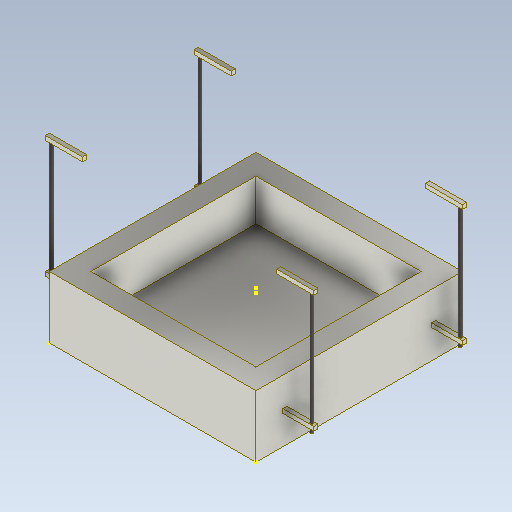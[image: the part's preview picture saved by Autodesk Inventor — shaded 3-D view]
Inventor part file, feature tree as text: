
AUTODESK INVENTOR PART (.ipt)
format: ipt  version: 2021 (Build 250183000, 183)  size: 241,152 bytes
history: native  units: mm
features: sketch x11, extrude x7, thread x7, pattern_linear x6
ambient origin geometry x8: Origin, YZ Plane, XZ Plane, XY Plane, X Axis, Y Axis, Z Axis, Center Point
bodies: Solid1 (feature_tree)
feature tree (31):
  extrude  "Extrusion1"  Depth=100.0mm
  extrude  "Extrusion2"  Depth=80.0mm
  sketch  "Sketch5"  dims[d7=80.0mm d8=20.0mm d9=0.0mm]
  extrude  "Extrusion5"  Depth=20.0mm TaperAngle=0.0deg
  pattern_linear  "Rectangular Pattern1"  Count1=2 Spacing1=115.0mm
  extrude  "Extrusion6"  Depth=55.0mm TaperAngle=0.0deg
  extrude  "Extrusion7"  Depth=2.0mm TaperAngle=0.0deg
  thread  "Thread1"  [1 undecoded]
  pattern_linear  "Rectangular Pattern2"  Count1=2 Spacing1=72.0mm
  pattern_linear  "Rectangular Pattern3"  Count1=2 Spacing1=126.0mm
  thread  "Thread2"  [1 undecoded]
  thread  "Thread3"  [1 undecoded]
  thread  "Thread4"  [1 undecoded]
  pattern_linear  "Rectangular Pattern4"  Count1=2 Spacing1=72.0mm
  thread  "Thread5"  [1 undecoded]
  thread  "Thread6"  [1 undecoded]
  thread  "Thread7"  [1 undecoded]
  sketch  "Sketch9"  dims[d25=2.0mm]
  sketch  "Sketch10"  dims[d26=15.0mm d27=0.0mm d28=20.0mm d30=115.0mm]
  extrude  "Extrusion8"  Depth=18.0mm
  sketch  "Sketch12"  dims[d34=1.5mm d35=2.0mm d36=0.0mm d37=59.0mm d38=0.0mm d39=20.0mm d41=72.0mm d42=20.0mm d44=126.0mm d45=55.0mm d46=0.0mm d47=55.0mm d48=0.0mm d49=55.0mm d50=0.0mm d51=20.0mm d53=72.0mm d54=20.0mm d56=126.0mm d57=2.0mm d58=0.0mm d59=2.0mm d60=0.0mm]
  extrude  "Extrusion9"  Depth=2.0mm TaperAngle=0.0deg
  pattern_linear  "Rectangular Pattern5"  Spacing1=18.0mm  [1 undecoded]
  pattern_linear  "Rectangular Pattern6"  Spacing1=2.0mm  [1 undecoded]
  sketch  "Sketch1"  dims[d0=100.0mm d1=100.0mm]
  sketch  "Sketch2"  dims[d2=30.0mm d3=0.0mm d6=80.0mm]
  sketch  "Sketch6"  dims[d22=2.0mm]
  sketch  "Sketch7"  dims[d23=2.0mm]
  sketch  "Sketch8"  dims[d24=2.0mm]
  sketch  "Sketch11"  dims[d31=1.5mm d32=55.0mm d33=0.0mm]
  sketch  "Sketch13"  dims[d61=2.0mm d62=0.0mm d63=18.0mm d64=2.0mm d65=0.0mm d66=18.0mm d67=2.0mm d68=2.0mm d69=0.0mm d70=20.0mm d72=72.0mm d73=20.0mm d75=72.0mm]
note: 9 required parameter values undecoded (feature->parameter linkage not recoverable at this tier; creation-order binding heuristic only, values carry confidence <= 0.55)
